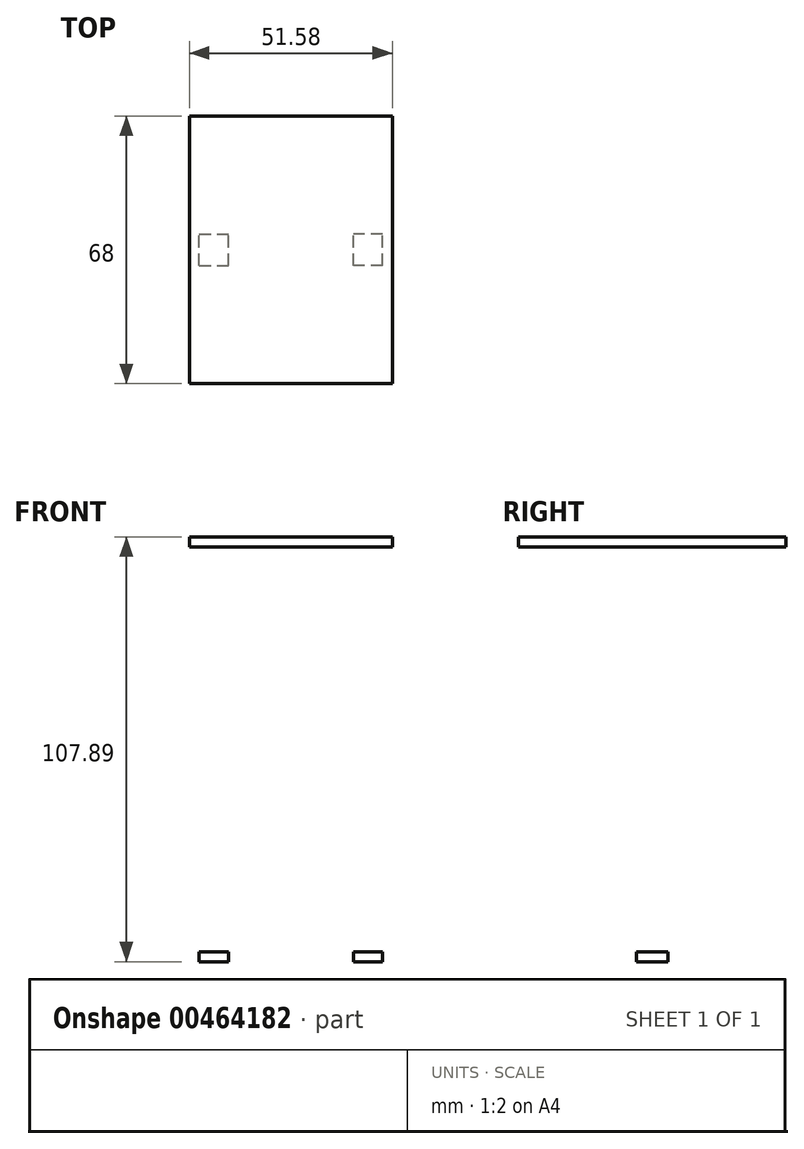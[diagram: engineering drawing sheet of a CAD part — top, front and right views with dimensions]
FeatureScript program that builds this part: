
annotation { "Feature Type Name" : "Feature", "Feature Type Description" : "" }
export const myFeature = defineFeature(function(context is Context, id is Id, definition is map)
    precondition{}
    {
        {
            var Q0;
            Q0=qCreatedBy(makeId("Front.planeOp"),FACE);
            var sketch = newSketch(context, id + "F0", { "sketchPlane" : qUnion([Q0])});
            skLineSegment(sketch, "E0.bottom", {"start": v(-71.3, 64.78) * mm, "end": v(-19.73, 64.78) * mm});
            skLineSegment(sketch, "E0.top", {"start": v(-71.3, 62.3) * mm, "end": v(-19.73, 62.3) * mm});
            skLineSegment(sketch, "E0.left", {"start": v(-71.3, 64.78) * mm, "end": v(-71.3, 62.3) * mm});
            skLineSegment(sketch, "E0.right", {"start": v(-19.73, 64.78) * mm, "end": v(-19.73, 62.3) * mm});
            skLineSegment(sketch, "E1.bottom", {"start": v(-19.73, 62.3) * mm, "end": v(-22.2, 62.3) * mm});
            skLineSegment(sketch, "E1.top", {"start": v(-19.73, -43.1) * mm, "end": v(-22.2, -43.1) * mm});
            skLineSegment(sketch, "E1.left", {"start": v(-19.73, 62.3) * mm, "end": v(-19.73, -43.1) * mm});
            skLineSegment(sketch, "E1.right", {"start": v(-22.2, 62.3) * mm, "end": v(-22.2, -43.1) * mm});
            skLineSegment(sketch, "E2.bottom", {"start": v(-71.3, 62.3) * mm, "end": v(-68.83, 62.3) * mm});
            skLineSegment(sketch, "E2.top", {"start": v(-71.3, -43.1) * mm, "end": v(-68.83, -43.1) * mm});
            skLineSegment(sketch, "E2.left", {"start": v(-71.3, 62.3) * mm, "end": v(-71.3, -43.1) * mm});
            skLineSegment(sketch, "E2.right", {"start": v(-68.83, 62.3) * mm, "end": v(-68.83, -43.1) * mm});
            skLineSegment(sketch, "E3.bottom", {"start": v(-68.83, -43.1) * mm, "end": v(-61.4, -43.1) * mm});
            skLineSegment(sketch, "E3.top", {"start": v(-68.83, -40.63) * mm, "end": v(-61.4, -40.63) * mm});
            skLineSegment(sketch, "E3.left", {"start": v(-68.83, -43.1) * mm, "end": v(-68.83, -40.63) * mm});
            skLineSegment(sketch, "E3.right", {"start": v(-61.4, -43.1) * mm, "end": v(-61.4, -40.63) * mm});
            skLineSegment(sketch, "E4.bottom", {"start": v(-22.2, -43.1) * mm, "end": v(-29.64, -43.1) * mm});
            skLineSegment(sketch, "E4.top", {"start": v(-22.2, -40.63) * mm, "end": v(-29.64, -40.63) * mm});
            skLineSegment(sketch, "E4.left", {"start": v(-22.2, -43.1) * mm, "end": v(-22.2, -40.63) * mm});
            skLineSegment(sketch, "E4.right", {"start": v(-29.64, -43.1) * mm, "end": v(-29.64, -40.63) * mm});
            skSolve(sketch);
        }
        {
            var Q0;
            Q0=makeQuery(id+"F0.imprint","IMPRINT",FACE,{"disambiguationData":[TD([[makeQuery(id+"F0.imprint","IMPRINT",EDGE,{"derivedFrom":sQuery(id+"F0.wireOp",EDGE,"E4.bottom")}),-1.0]])]});
            var Q1;
            Q1=makeQuery(id+"F0.imprint","IMPRINT",FACE,{"disambiguationData":[TD([[makeQuery(id+"F0.imprint","IMPRINT",EDGE,{"derivedFrom":sQuery(id+"F0.wireOp",EDGE,"E1.bottom")}),1.0]])]});
            var Q2;
            Q2=makeQuery(id+"F0.imprint","IMPRINT",FACE,{"disambiguationData":[TD([[makeQuery(id+"F0.imprint","IMPRINT",EDGE,{"derivedFrom":sQuery(id+"F0.wireOp",EDGE,"E0.bottom")}),-1.0]])]});
            var Q3;
            Q3=makeQuery(id+"F0.imprint","IMPRINT",FACE,{"disambiguationData":[TD([[makeQuery(id+"F0.imprint","IMPRINT",EDGE,{"derivedFrom":sQuery(id+"F0.wireOp",EDGE,"E2.bottom")}),-1.0]])]});
            var Q4;
            Q4=makeQuery(id+"F0.imprint","IMPRINT",FACE,{"disambiguationData":[TD([[makeQuery(id+"F0.imprint","IMPRINT",EDGE,{"derivedFrom":sQuery(id+"F0.wireOp",EDGE,"E3.bottom")}),1.0]])]});
            extrude(context, id + "F1", {"entities" : qUnion([Q0, Q1, Q2, Q3, Q4]), "depth" : 8 * mm});
        }
        {
            var Q0;
            Q0=makeQuery(id+"F1.opExtrude","CAP_FACE",FACE,{"disambiguationData":[OSD([sQuery(id+"F0.wireOp",EDGE,"E0.bottom"),sQuery(id+"F0.wireOp",EDGE,"E0.top"),sQuery(id+"F0.wireOp",EDGE,"E0.left"),sQuery(id+"F0.wireOp",EDGE,"E0.right"),sQuery(id+"F0.wireOp",EDGE,"E1.top"),sQuery(id+"F0.wireOp",EDGE,"E1.left"),sQuery(id+"F0.wireOp",EDGE,"E1.right"),sQuery(id+"F0.wireOp",EDGE,"E2.top"),sQuery(id+"F0.wireOp",EDGE,"E2.left"),sQuery(id+"F0.wireOp",EDGE,"E2.right"),sQuery(id+"F0.wireOp",EDGE,"E3.bottom"),sQuery(id+"F0.wireOp",EDGE,"E3.top"),sQuery(id+"F0.wireOp",EDGE,"E3.right"),sQuery(id+"F0.wireOp",EDGE,"E4.bottom"),sQuery(id+"F0.wireOp",EDGE,"E4.top"),sQuery(id+"F0.wireOp",EDGE,"E4.right")])],"isStart":true});
            var sketch = newSketch(context, id + "F2", { "sketchPlane" : qUnion([Q0])});
            skLineSegment(sketch, "E5.bottom", {"start": v(19.73, 64.78) * mm, "end": v(71.3, 64.78) * mm});
            skLineSegment(sketch, "E5.top", {"start": v(19.73, 62.3) * mm, "end": v(71.3, 62.3) * mm});
            skLineSegment(sketch, "E5.left", {"start": v(19.73, 64.78) * mm, "end": v(19.73, 62.3) * mm});
            skLineSegment(sketch, "E5.right", {"start": v(71.3, 64.78) * mm, "end": v(71.3, 62.3) * mm});
            skSolve(sketch);
        }
        {
            var Q0;
            Q0=makeQuery(id+"F2.imprint","IMPRINT",FACE,{"disambiguationData":[TD([[makeQuery(id+"F2.imprint","IMPRINT",EDGE,{"derivedFrom":sQuery(id+"F2.wireOp",EDGE,"E5.bottom")}),1.0]])]});
            extrude(context, id + "F3", {"entities" : qUnion([Q0]), "operationType" : NewBodyOperationType.ADD, "depth" : 30 * mm});
        }
        {
            var Q0;
            Q0=makeQuery(id+"F1.opExtrude","CAP_FACE",FACE,{"disambiguationData":[OSD([sQuery(id+"F0.wireOp",EDGE,"E0.bottom"),sQuery(id+"F0.wireOp",EDGE,"E0.top"),sQuery(id+"F0.wireOp",EDGE,"E0.left"),sQuery(id+"F0.wireOp",EDGE,"E0.right"),sQuery(id+"F0.wireOp",EDGE,"E1.top"),sQuery(id+"F0.wireOp",EDGE,"E1.left"),sQuery(id+"F0.wireOp",EDGE,"E1.right"),sQuery(id+"F0.wireOp",EDGE,"E2.top"),sQuery(id+"F0.wireOp",EDGE,"E2.left"),sQuery(id+"F0.wireOp",EDGE,"E2.right"),sQuery(id+"F0.wireOp",EDGE,"E3.bottom"),sQuery(id+"F0.wireOp",EDGE,"E3.top"),sQuery(id+"F0.wireOp",EDGE,"E3.right"),sQuery(id+"F0.wireOp",EDGE,"E4.bottom"),sQuery(id+"F0.wireOp",EDGE,"E4.top"),sQuery(id+"F0.wireOp",EDGE,"E4.right")])],"isStart":false});
            var sketch = newSketch(context, id + "F4", { "sketchPlane" : qUnion([Q0])});
            skLineSegment(sketch, "E6.bottom", {"start": v(-71.3, 64.78) * mm, "end": v(-19.73, 64.78) * mm});
            skLineSegment(sketch, "E6.top", {"start": v(-71.3, 62.3) * mm, "end": v(-19.73, 62.3) * mm});
            skLineSegment(sketch, "E6.left", {"start": v(-71.3, 64.78) * mm, "end": v(-71.3, 62.3) * mm});
            skLineSegment(sketch, "E6.right", {"start": v(-19.73, 64.78) * mm, "end": v(-19.73, 62.3) * mm});
            skSolve(sketch);
        }
        {
            var Q0;
            Q0=makeQuery(id+"F4.imprint","IMPRINT",FACE,{"disambiguationData":[TD([[makeQuery(id+"F4.imprint","IMPRINT",EDGE,{"derivedFrom":sQuery(id+"F4.wireOp",EDGE,"E6.bottom")}),-1.0]])]});
            extrude(context, id + "F5", {"entities" : qUnion([Q0]), "operationType" : NewBodyOperationType.ADD, "depth" : 30 * mm});
        }
    });
